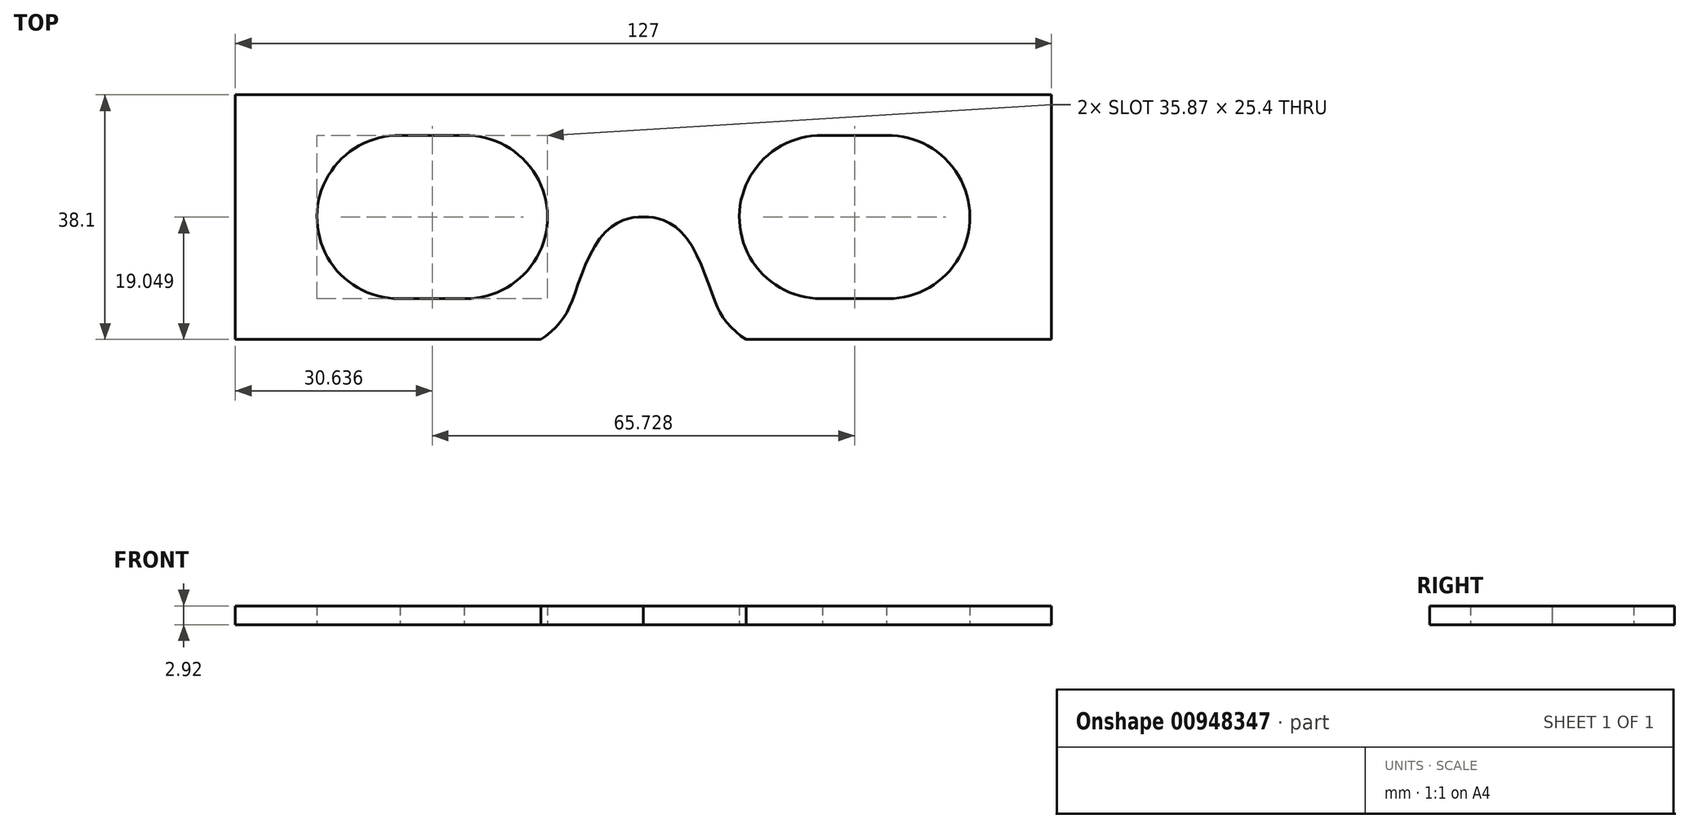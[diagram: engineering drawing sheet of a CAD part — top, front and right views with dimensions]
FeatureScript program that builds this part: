
annotation { "Feature Type Name" : "Feature", "Feature Type Description" : "" }
export const myFeature = defineFeature(function(context is Context, id is Id, definition is map)
    precondition{}
    {
        {
            var Q0;
            Q0=qCreatedBy(makeId("Top.planeOp"),FACE);
            var sketch = newSketch(context, id + "F0", { "sketchPlane" : qUnion([Q0])});
            skLineSegment(sketch, "E0.bottom", {"start": v(0, 0) * mm, "end": v(-63.5, 0) * mm});
            skLineSegment(sketch, "E0.top", {"start": v(0, 38.1) * mm, "end": v(-63.5, 38.1) * mm});
            skLineSegment(sketch, "E0.left", {"start": v(0, 0) * mm, "end": v(0, 38.1) * mm});
            skLineSegment(sketch, "E0.right", {"start": v(-63.5, 0) * mm, "end": v(-63.5, 38.1) * mm});
            skCircle(sketch, "E1", {"center": v(-38.1, 19.05) * mm, "radius": 12.7 * mm});
            skLineSegment(sketch, "E2", {"start": v(-38.1, 19.05) * mm, "end": v(-38.1, 0) * mm});
            skFitSpline(sketch, "E3", {"points": [v(0, 19.05) * mm, v(-2.63, 18.75) * mm, v(-6.82, 15.67) * mm, v(-10.88, 6.6) * mm, v(-12.79, 2.86) * mm, v(-15.97, 0) * mm], "startDerivative": vector(-19.51, 0.46) * mm, "endDerivative": vector(-17.53, -11) * mm});
            skCircle(sketch, "E4", {"center": v(-27.63, 19.05) * mm, "radius": 12.7 * mm});
            skLineSegment(sketch, "E5", {"start": v(-37.86, 31.75) * mm, "end": v(-27.39, 31.75) * mm});
            skLineSegment(sketch, "E6", {"start": v(-38.1, 6.35) * mm, "end": v(-27.63, 6.35) * mm});
            skSolve(sketch);
        }
        {
            var Q0;
            {var subQ1=sQuery(id+"F0.wireOp",EDGE,"E0.top");Q0=makeQuery(id+"F0.imprint","IMPRINT",FACE,{"disambiguationData":[TD([[makeQuery(id+"F0.imprint","IMPRINT",EDGE,{"derivedFrom":subQ1}),1.0]])]});}
            var Q1;
            {var subQ5=sQuery(id+"F0.wireOp",EDGE,"E0.right");var subQ6=sQuery(id+"F0.wireOp",EDGE,"E0.bottom");var subQ7=makeQuery(id+"F0.imprint","INTERSECT",VERTEX,{"derivedFrom":[subQ6,subQ5]});Q1=makeQuery(id+"F0.imprint","IMPRINT",FACE,{"disambiguationData":[TD([[makeQuery(id+"F0.imprint","IMPRINT",EDGE,{"disambiguationData":[TD([[subQ7,1.0]])],"derivedFrom":subQ6}),-1.0]])]});}
            var Q2;
            {var subQ7=sQuery(id+"F0.wireOp",EDGE,"E3");Q2=makeQuery(id+"F0.imprint","IMPRINT",FACE,{"disambiguationData":[TD([[makeQuery(id+"F0.imprint","IMPRINT",EDGE,{"derivedFrom":subQ7}),-1.0]])]});}
            var Q3;
            {var subQ5=sQuery(id+"F0.wireOp",EDGE,"E6");Q3=makeQuery(id+"F0.imprint","IMPRINT",FACE,{"disambiguationData":[TD([[makeQuery(id+"F0.imprint","IMPRINT",EDGE,{"derivedFrom":subQ5}),-1.0]])]});}
            extrude(context, id + "F1", {"entities" : qUnion([Q0, Q1, Q2, Q3]), "depth" : 2.92 * mm, "offsetDistance" : 25.4 * mm});
        }
        {
            var Q0;
            Q0=makeQuery(id+"F1.opExtrude","SWEPT_BODY",BODY,{"disambiguationData":[OSD([sQuery(id+"F0.wireOp",EDGE,"E0.bottom"),sQuery(id+"F0.wireOp",EDGE,"E0.top"),sQuery(id+"F0.wireOp",EDGE,"E0.left"),sQuery(id+"F0.wireOp",EDGE,"E0.right"),sQuery(id+"F0.wireOp",EDGE,"E1"),sQuery(id+"F0.wireOp",EDGE,"E3")])]});
            var Q1;
            Q1=qCreatedBy(makeId("Right.planeOp"),FACE);
            mirror(context, id + "F2", {"operationType" : NewBodyOperationType.ADD, "entities" : qUnion([Q0]), "mirrorPlane" : qUnion([Q1])});
        }
    });
